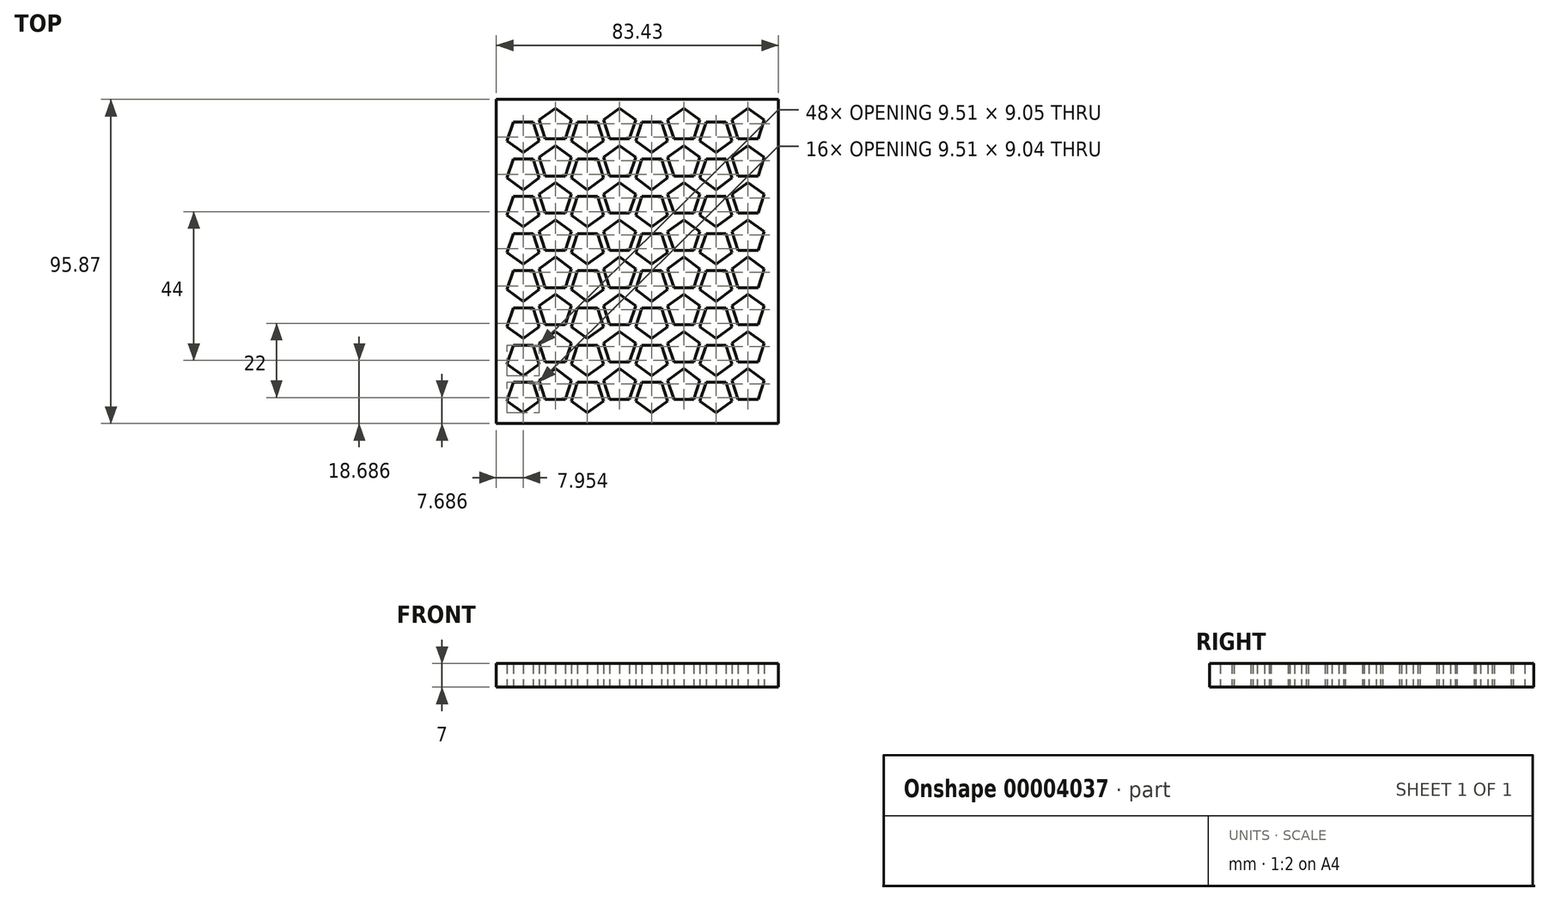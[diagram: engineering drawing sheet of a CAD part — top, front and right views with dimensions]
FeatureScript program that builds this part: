
annotation { "Feature Type Name" : "Feature", "Feature Type Description" : "" }
export const myFeature = defineFeature(function(context is Context, id is Id, definition is map)
    precondition{}
    {
        {
            var Q0;
            Q0=qCreatedBy(makeId("Top.planeOp"),FACE);
            var sketch = newSketch(context, id + "F0", { "sketchPlane" : qUnion([Q0])});
            skLineSegment(sketch, "E0.bottom", {"start": v(-101.75, 60.18) * mm, "end": v(-18.32, 60.18) * mm});
            skLineSegment(sketch, "E0.top", {"start": v(-101.75, -35.69) * mm, "end": v(-18.32, -35.69) * mm});
            skLineSegment(sketch, "E0.left", {"start": v(-101.75, 60.18) * mm, "end": v(-101.75, -35.69) * mm});
            skLineSegment(sketch, "E0.right", {"start": v(-18.32, 60.18) * mm, "end": v(-18.32, -35.69) * mm});
            skCircle(sketch, "E1.cCircle", {"center": v(-93.8, 49.47) * mm, "radius": 5 * mm, "construction": true});
            skLineSegment(sketch, "E1.0", {"start": v(-93.8, 44.47) * mm, "end": v(-98.55, 47.93) * mm});
            skLineSegment(sketch, "E1.1", {"start": v(-98.55, 47.93) * mm, "end": v(-96.73, 53.52) * mm});
            skLineSegment(sketch, "E1.2", {"start": v(-96.73, 53.52) * mm, "end": v(-90.86, 53.52) * mm});
            skLineSegment(sketch, "E1.3", {"start": v(-90.86, 53.52) * mm, "end": v(-89.04, 47.93) * mm});
            skLineSegment(sketch, "E1.4", {"start": v(-89.04, 47.93) * mm, "end": v(-93.8, 44.47) * mm});
            skLineSegment(sketch, "E2", {"start": v(-93.8, 49.47) * mm, "end": v(-93.8, 0) * mm, "construction": true});
            skCircle(sketch, "E3.cCircle", {"center": v(-84.3, 52.56) * mm, "radius": 5 * mm, "construction": true});
            skLineSegment(sketch, "E3.0", {"start": v(-87.23, 48.51) * mm, "end": v(-89.05, 54.1) * mm});
            skLineSegment(sketch, "E3.1", {"start": v(-89.05, 54.1) * mm, "end": v(-84.3, 57.56) * mm});
            skLineSegment(sketch, "E3.2", {"start": v(-84.3, 57.56) * mm, "end": v(-79.54, 54.1) * mm});
            skLineSegment(sketch, "E3.3", {"start": v(-79.54, 54.1) * mm, "end": v(-81.36, 48.51) * mm});
            skLineSegment(sketch, "E3.4", {"start": v(-81.36, 48.51) * mm, "end": v(-87.23, 48.51) * mm});
            skLineSegment(sketch, "E4", {"start": v(-93.8, 49.47) * mm, "end": v(-84.3, 52.56) * mm, "construction": true});
            skLineSegment(sketch, "E5", {"start": v(-90.86, 53.52) * mm, "end": v(-89.05, 54.1) * mm, "construction": true});
            skLineSegment(sketch, "E6.0.1.0", {"start": v(-98.55, 36.93) * mm, "end": v(-96.73, 42.52) * mm});
            skLineSegment(sketch, "E6.0.1.1", {"start": v(-96.73, 42.52) * mm, "end": v(-90.86, 42.52) * mm});
            skLineSegment(sketch, "E6.0.1.2", {"start": v(-90.86, 42.52) * mm, "end": v(-89.04, 36.93) * mm});
            skLineSegment(sketch, "E6.0.1.3", {"start": v(-89.04, 36.93) * mm, "end": v(-93.8, 33.47) * mm});
            skLineSegment(sketch, "E6.0.1.4", {"start": v(-93.8, 33.47) * mm, "end": v(-98.55, 36.93) * mm});
            skLineSegment(sketch, "E6.0.1.5", {"start": v(-87.23, 37.51) * mm, "end": v(-89.05, 43.1) * mm});
            skLineSegment(sketch, "E6.0.1.6", {"start": v(-89.05, 43.1) * mm, "end": v(-84.3, 46.56) * mm});
            skLineSegment(sketch, "E6.0.1.7", {"start": v(-84.3, 46.56) * mm, "end": v(-79.54, 43.1) * mm});
            skLineSegment(sketch, "E6.0.1.8", {"start": v(-79.54, 43.1) * mm, "end": v(-81.36, 37.51) * mm});
            skLineSegment(sketch, "E6.0.1.9", {"start": v(-81.36, 37.51) * mm, "end": v(-87.23, 37.51) * mm});
            skLineSegment(sketch, "E6.0.2.0", {"start": v(-98.55, 25.93) * mm, "end": v(-96.73, 31.52) * mm});
            skLineSegment(sketch, "E6.0.2.1", {"start": v(-96.73, 31.52) * mm, "end": v(-90.86, 31.52) * mm});
            skLineSegment(sketch, "E6.0.2.2", {"start": v(-90.86, 31.52) * mm, "end": v(-89.04, 25.93) * mm});
            skLineSegment(sketch, "E6.0.2.3", {"start": v(-89.04, 25.93) * mm, "end": v(-93.8, 22.47) * mm});
            skLineSegment(sketch, "E6.0.2.4", {"start": v(-93.8, 22.47) * mm, "end": v(-98.55, 25.93) * mm});
            skLineSegment(sketch, "E6.0.2.5", {"start": v(-87.23, 26.51) * mm, "end": v(-89.05, 32.1) * mm});
            skLineSegment(sketch, "E6.0.2.6", {"start": v(-89.05, 32.1) * mm, "end": v(-84.3, 35.56) * mm});
            skLineSegment(sketch, "E6.0.2.7", {"start": v(-84.3, 35.56) * mm, "end": v(-79.54, 32.1) * mm});
            skLineSegment(sketch, "E6.0.2.8", {"start": v(-79.54, 32.1) * mm, "end": v(-81.36, 26.51) * mm});
            skLineSegment(sketch, "E6.0.2.9", {"start": v(-81.36, 26.51) * mm, "end": v(-87.23, 26.51) * mm});
            skLineSegment(sketch, "E6.0.3.0", {"start": v(-98.55, 14.93) * mm, "end": v(-96.73, 20.52) * mm});
            skLineSegment(sketch, "E6.0.3.1", {"start": v(-96.73, 20.52) * mm, "end": v(-90.86, 20.52) * mm});
            skLineSegment(sketch, "E6.0.3.2", {"start": v(-90.86, 20.52) * mm, "end": v(-89.04, 14.93) * mm});
            skLineSegment(sketch, "E6.0.3.3", {"start": v(-89.04, 14.93) * mm, "end": v(-93.8, 11.47) * mm});
            skLineSegment(sketch, "E6.0.3.4", {"start": v(-93.8, 11.47) * mm, "end": v(-98.55, 14.93) * mm});
            skLineSegment(sketch, "E6.0.3.5", {"start": v(-87.23, 15.51) * mm, "end": v(-89.05, 21.1) * mm});
            skLineSegment(sketch, "E6.0.3.6", {"start": v(-89.05, 21.1) * mm, "end": v(-84.3, 24.56) * mm});
            skLineSegment(sketch, "E6.0.3.7", {"start": v(-84.3, 24.56) * mm, "end": v(-79.54, 21.1) * mm});
            skLineSegment(sketch, "E6.0.3.8", {"start": v(-79.54, 21.1) * mm, "end": v(-81.36, 15.51) * mm});
            skLineSegment(sketch, "E6.0.3.9", {"start": v(-81.36, 15.51) * mm, "end": v(-87.23, 15.51) * mm});
            skLineSegment(sketch, "E6.0.4.0", {"start": v(-98.55, 3.93) * mm, "end": v(-96.73, 9.52) * mm});
            skLineSegment(sketch, "E6.0.4.1", {"start": v(-96.73, 9.52) * mm, "end": v(-90.86, 9.52) * mm});
            skLineSegment(sketch, "E6.0.4.2", {"start": v(-90.86, 9.52) * mm, "end": v(-89.04, 3.93) * mm});
            skLineSegment(sketch, "E6.0.4.3", {"start": v(-89.04, 3.93) * mm, "end": v(-93.8, 0.47) * mm});
            skLineSegment(sketch, "E6.0.4.4", {"start": v(-93.8, 0.47) * mm, "end": v(-98.55, 3.93) * mm});
            skLineSegment(sketch, "E6.0.4.5", {"start": v(-87.23, 4.51) * mm, "end": v(-89.05, 10.1) * mm});
            skLineSegment(sketch, "E6.0.4.6", {"start": v(-89.05, 10.1) * mm, "end": v(-84.3, 13.56) * mm});
            skLineSegment(sketch, "E6.0.4.7", {"start": v(-84.3, 13.56) * mm, "end": v(-79.54, 10.1) * mm});
            skLineSegment(sketch, "E6.0.4.8", {"start": v(-79.54, 10.1) * mm, "end": v(-81.36, 4.51) * mm});
            skLineSegment(sketch, "E6.0.4.9", {"start": v(-81.36, 4.51) * mm, "end": v(-87.23, 4.51) * mm});
            skLineSegment(sketch, "E6.0.5.0", {"start": v(-98.55, -7.07) * mm, "end": v(-96.73, -1.48) * mm});
            skLineSegment(sketch, "E6.0.5.1", {"start": v(-96.73, -1.48) * mm, "end": v(-90.86, -1.48) * mm});
            skLineSegment(sketch, "E6.0.5.2", {"start": v(-90.86, -1.48) * mm, "end": v(-89.04, -7.07) * mm});
            skLineSegment(sketch, "E6.0.5.3", {"start": v(-89.04, -7.07) * mm, "end": v(-93.8, -10.53) * mm});
            skLineSegment(sketch, "E6.0.5.4", {"start": v(-93.8, -10.53) * mm, "end": v(-98.55, -7.07) * mm});
            skLineSegment(sketch, "E6.0.5.5", {"start": v(-87.23, -6.49) * mm, "end": v(-89.05, -0.9) * mm});
            skLineSegment(sketch, "E6.0.5.6", {"start": v(-89.05, -0.9) * mm, "end": v(-84.3, 2.56) * mm});
            skLineSegment(sketch, "E6.0.5.7", {"start": v(-84.3, 2.56) * mm, "end": v(-79.54, -0.9) * mm});
            skLineSegment(sketch, "E6.0.5.8", {"start": v(-79.54, -0.9) * mm, "end": v(-81.36, -6.49) * mm});
            skLineSegment(sketch, "E6.0.5.9", {"start": v(-81.36, -6.49) * mm, "end": v(-87.23, -6.49) * mm});
            skLineSegment(sketch, "E6.0.6.0", {"start": v(-98.55, -18.07) * mm, "end": v(-96.73, -12.48) * mm});
            skLineSegment(sketch, "E6.0.6.1", {"start": v(-96.73, -12.48) * mm, "end": v(-90.86, -12.48) * mm});
            skLineSegment(sketch, "E6.0.6.2", {"start": v(-90.86, -12.48) * mm, "end": v(-89.04, -18.07) * mm});
            skLineSegment(sketch, "E6.0.6.3", {"start": v(-89.04, -18.07) * mm, "end": v(-93.8, -21.53) * mm});
            skLineSegment(sketch, "E6.0.6.4", {"start": v(-93.8, -21.53) * mm, "end": v(-98.55, -18.07) * mm});
            skLineSegment(sketch, "E6.0.6.5", {"start": v(-87.23, -17.49) * mm, "end": v(-89.05, -11.9) * mm});
            skLineSegment(sketch, "E6.0.6.6", {"start": v(-89.05, -11.9) * mm, "end": v(-84.3, -8.44) * mm});
            skLineSegment(sketch, "E6.0.6.7", {"start": v(-84.3, -8.44) * mm, "end": v(-79.54, -11.9) * mm});
            skLineSegment(sketch, "E6.0.6.8", {"start": v(-79.54, -11.9) * mm, "end": v(-81.36, -17.49) * mm});
            skLineSegment(sketch, "E6.0.6.9", {"start": v(-81.36, -17.49) * mm, "end": v(-87.23, -17.49) * mm});
            skLineSegment(sketch, "E6.0.7.0", {"start": v(-98.55, -29.07) * mm, "end": v(-96.73, -23.48) * mm});
            skLineSegment(sketch, "E6.0.7.1", {"start": v(-96.73, -23.48) * mm, "end": v(-90.86, -23.48) * mm});
            skLineSegment(sketch, "E6.0.7.2", {"start": v(-90.86, -23.48) * mm, "end": v(-89.04, -29.07) * mm});
            skLineSegment(sketch, "E6.0.7.3", {"start": v(-89.04, -29.07) * mm, "end": v(-93.8, -32.53) * mm});
            skLineSegment(sketch, "E6.0.7.4", {"start": v(-93.8, -32.53) * mm, "end": v(-98.55, -29.07) * mm});
            skLineSegment(sketch, "E6.0.7.5", {"start": v(-87.23, -28.49) * mm, "end": v(-89.05, -22.9) * mm});
            skLineSegment(sketch, "E6.0.7.6", {"start": v(-89.05, -22.9) * mm, "end": v(-84.3, -19.44) * mm});
            skLineSegment(sketch, "E6.0.7.7", {"start": v(-84.3, -19.44) * mm, "end": v(-79.54, -22.9) * mm});
            skLineSegment(sketch, "E6.0.7.8", {"start": v(-79.54, -22.9) * mm, "end": v(-81.36, -28.49) * mm});
            skLineSegment(sketch, "E6.0.7.9", {"start": v(-81.36, -28.49) * mm, "end": v(-87.23, -28.49) * mm});
            skLineSegment(sketch, "E6.1.0.0", {"start": v(-79.55, 47.93) * mm, "end": v(-77.73, 53.52) * mm});
            skLineSegment(sketch, "E6.1.0.1", {"start": v(-77.73, 53.52) * mm, "end": v(-71.86, 53.52) * mm});
            skLineSegment(sketch, "E6.1.0.2", {"start": v(-71.86, 53.52) * mm, "end": v(-70.04, 47.93) * mm});
            skLineSegment(sketch, "E6.1.0.3", {"start": v(-70.04, 47.93) * mm, "end": v(-74.8, 44.47) * mm});
            skLineSegment(sketch, "E6.1.0.4", {"start": v(-74.8, 44.47) * mm, "end": v(-79.55, 47.93) * mm});
            skLineSegment(sketch, "E6.1.0.5", {"start": v(-68.23, 48.51) * mm, "end": v(-70.05, 54.1) * mm});
            skLineSegment(sketch, "E6.1.0.6", {"start": v(-70.05, 54.1) * mm, "end": v(-65.3, 57.56) * mm});
            skLineSegment(sketch, "E6.1.0.7", {"start": v(-65.3, 57.56) * mm, "end": v(-60.54, 54.1) * mm});
            skLineSegment(sketch, "E6.1.0.8", {"start": v(-60.54, 54.1) * mm, "end": v(-62.36, 48.51) * mm});
            skLineSegment(sketch, "E6.1.0.9", {"start": v(-62.36, 48.51) * mm, "end": v(-68.23, 48.51) * mm});
            skLineSegment(sketch, "E6.1.1.0", {"start": v(-79.55, 36.93) * mm, "end": v(-77.73, 42.52) * mm});
            skLineSegment(sketch, "E6.1.1.1", {"start": v(-77.73, 42.52) * mm, "end": v(-71.86, 42.52) * mm});
            skLineSegment(sketch, "E6.1.1.2", {"start": v(-71.86, 42.52) * mm, "end": v(-70.04, 36.93) * mm});
            skLineSegment(sketch, "E6.1.1.3", {"start": v(-70.04, 36.93) * mm, "end": v(-74.8, 33.47) * mm});
            skLineSegment(sketch, "E6.1.1.4", {"start": v(-74.8, 33.47) * mm, "end": v(-79.55, 36.93) * mm});
            skLineSegment(sketch, "E6.1.1.5", {"start": v(-68.23, 37.51) * mm, "end": v(-70.05, 43.1) * mm});
            skLineSegment(sketch, "E6.1.1.6", {"start": v(-70.05, 43.1) * mm, "end": v(-65.3, 46.56) * mm});
            skLineSegment(sketch, "E6.1.1.7", {"start": v(-65.3, 46.56) * mm, "end": v(-60.54, 43.1) * mm});
            skLineSegment(sketch, "E6.1.1.8", {"start": v(-60.54, 43.1) * mm, "end": v(-62.36, 37.51) * mm});
            skLineSegment(sketch, "E6.1.1.9", {"start": v(-62.36, 37.51) * mm, "end": v(-68.23, 37.51) * mm});
            skLineSegment(sketch, "E6.1.2.0", {"start": v(-79.55, 25.93) * mm, "end": v(-77.73, 31.52) * mm});
            skLineSegment(sketch, "E6.1.2.1", {"start": v(-77.73, 31.52) * mm, "end": v(-71.86, 31.52) * mm});
            skLineSegment(sketch, "E6.1.2.2", {"start": v(-71.86, 31.52) * mm, "end": v(-70.04, 25.93) * mm});
            skLineSegment(sketch, "E6.1.2.3", {"start": v(-70.04, 25.93) * mm, "end": v(-74.8, 22.47) * mm});
            skLineSegment(sketch, "E6.1.2.4", {"start": v(-74.8, 22.47) * mm, "end": v(-79.55, 25.93) * mm});
            skLineSegment(sketch, "E6.1.2.5", {"start": v(-68.23, 26.51) * mm, "end": v(-70.05, 32.1) * mm});
            skLineSegment(sketch, "E6.1.2.6", {"start": v(-70.05, 32.1) * mm, "end": v(-65.3, 35.56) * mm});
            skLineSegment(sketch, "E6.1.2.7", {"start": v(-65.3, 35.56) * mm, "end": v(-60.54, 32.1) * mm});
            skLineSegment(sketch, "E6.1.2.8", {"start": v(-60.54, 32.1) * mm, "end": v(-62.36, 26.51) * mm});
            skLineSegment(sketch, "E6.1.2.9", {"start": v(-62.36, 26.51) * mm, "end": v(-68.23, 26.51) * mm});
            skLineSegment(sketch, "E6.1.3.0", {"start": v(-79.55, 14.93) * mm, "end": v(-77.73, 20.52) * mm});
            skLineSegment(sketch, "E6.1.3.1", {"start": v(-77.73, 20.52) * mm, "end": v(-71.86, 20.52) * mm});
            skLineSegment(sketch, "E6.1.3.2", {"start": v(-71.86, 20.52) * mm, "end": v(-70.04, 14.93) * mm});
            skLineSegment(sketch, "E6.1.3.3", {"start": v(-70.04, 14.93) * mm, "end": v(-74.8, 11.47) * mm});
            skLineSegment(sketch, "E6.1.3.4", {"start": v(-74.8, 11.47) * mm, "end": v(-79.55, 14.93) * mm});
            skLineSegment(sketch, "E6.1.3.5", {"start": v(-68.23, 15.51) * mm, "end": v(-70.05, 21.1) * mm});
            skLineSegment(sketch, "E6.1.3.6", {"start": v(-70.05, 21.1) * mm, "end": v(-65.3, 24.56) * mm});
            skLineSegment(sketch, "E6.1.3.7", {"start": v(-65.3, 24.56) * mm, "end": v(-60.54, 21.1) * mm});
            skLineSegment(sketch, "E6.1.3.8", {"start": v(-60.54, 21.1) * mm, "end": v(-62.36, 15.51) * mm});
            skLineSegment(sketch, "E6.1.3.9", {"start": v(-62.36, 15.51) * mm, "end": v(-68.23, 15.51) * mm});
            skLineSegment(sketch, "E6.1.4.0", {"start": v(-79.55, 3.93) * mm, "end": v(-77.73, 9.52) * mm});
            skLineSegment(sketch, "E6.1.4.1", {"start": v(-77.73, 9.52) * mm, "end": v(-71.86, 9.52) * mm});
            skLineSegment(sketch, "E6.1.4.2", {"start": v(-71.86, 9.52) * mm, "end": v(-70.04, 3.93) * mm});
            skLineSegment(sketch, "E6.1.4.3", {"start": v(-70.04, 3.93) * mm, "end": v(-74.8, 0.47) * mm});
            skLineSegment(sketch, "E6.1.4.4", {"start": v(-74.8, 0.47) * mm, "end": v(-79.55, 3.93) * mm});
            skLineSegment(sketch, "E6.1.4.5", {"start": v(-68.23, 4.51) * mm, "end": v(-70.05, 10.1) * mm});
            skLineSegment(sketch, "E6.1.4.6", {"start": v(-70.05, 10.1) * mm, "end": v(-65.3, 13.56) * mm});
            skLineSegment(sketch, "E6.1.4.7", {"start": v(-65.3, 13.56) * mm, "end": v(-60.54, 10.1) * mm});
            skLineSegment(sketch, "E6.1.4.8", {"start": v(-60.54, 10.1) * mm, "end": v(-62.36, 4.51) * mm});
            skLineSegment(sketch, "E6.1.4.9", {"start": v(-62.36, 4.51) * mm, "end": v(-68.23, 4.51) * mm});
            skLineSegment(sketch, "E6.1.5.0", {"start": v(-79.55, -7.07) * mm, "end": v(-77.73, -1.48) * mm});
            skLineSegment(sketch, "E6.1.5.1", {"start": v(-77.73, -1.48) * mm, "end": v(-71.86, -1.48) * mm});
            skLineSegment(sketch, "E6.1.5.2", {"start": v(-71.86, -1.48) * mm, "end": v(-70.04, -7.07) * mm});
            skLineSegment(sketch, "E6.1.5.3", {"start": v(-70.04, -7.07) * mm, "end": v(-74.8, -10.53) * mm});
            skLineSegment(sketch, "E6.1.5.4", {"start": v(-74.8, -10.53) * mm, "end": v(-79.55, -7.07) * mm});
            skLineSegment(sketch, "E6.1.5.5", {"start": v(-68.23, -6.49) * mm, "end": v(-70.05, -0.9) * mm});
            skLineSegment(sketch, "E6.1.5.6", {"start": v(-70.05, -0.9) * mm, "end": v(-65.3, 2.56) * mm});
            skLineSegment(sketch, "E6.1.5.7", {"start": v(-65.3, 2.56) * mm, "end": v(-60.54, -0.9) * mm});
            skLineSegment(sketch, "E6.1.5.8", {"start": v(-60.54, -0.9) * mm, "end": v(-62.36, -6.49) * mm});
            skLineSegment(sketch, "E6.1.5.9", {"start": v(-62.36, -6.49) * mm, "end": v(-68.23, -6.49) * mm});
            skLineSegment(sketch, "E6.1.6.0", {"start": v(-79.55, -18.07) * mm, "end": v(-77.73, -12.48) * mm});
            skLineSegment(sketch, "E6.1.6.1", {"start": v(-77.73, -12.48) * mm, "end": v(-71.86, -12.48) * mm});
            skLineSegment(sketch, "E6.1.6.2", {"start": v(-71.86, -12.48) * mm, "end": v(-70.04, -18.07) * mm});
            skLineSegment(sketch, "E6.1.6.3", {"start": v(-70.04, -18.07) * mm, "end": v(-74.8, -21.53) * mm});
            skLineSegment(sketch, "E6.1.6.4", {"start": v(-74.8, -21.53) * mm, "end": v(-79.55, -18.07) * mm});
            skLineSegment(sketch, "E6.1.6.5", {"start": v(-68.23, -17.49) * mm, "end": v(-70.05, -11.9) * mm});
            skLineSegment(sketch, "E6.1.6.6", {"start": v(-70.05, -11.9) * mm, "end": v(-65.3, -8.44) * mm});
            skLineSegment(sketch, "E6.1.6.7", {"start": v(-65.3, -8.44) * mm, "end": v(-60.54, -11.9) * mm});
            skLineSegment(sketch, "E6.1.6.8", {"start": v(-60.54, -11.9) * mm, "end": v(-62.36, -17.49) * mm});
            skLineSegment(sketch, "E6.1.6.9", {"start": v(-62.36, -17.49) * mm, "end": v(-68.23, -17.49) * mm});
            skLineSegment(sketch, "E6.1.7.0", {"start": v(-79.55, -29.07) * mm, "end": v(-77.73, -23.48) * mm});
            skLineSegment(sketch, "E6.1.7.1", {"start": v(-77.73, -23.48) * mm, "end": v(-71.86, -23.48) * mm});
            skLineSegment(sketch, "E6.1.7.2", {"start": v(-71.86, -23.48) * mm, "end": v(-70.04, -29.07) * mm});
            skLineSegment(sketch, "E6.1.7.3", {"start": v(-70.04, -29.07) * mm, "end": v(-74.8, -32.53) * mm});
            skLineSegment(sketch, "E6.1.7.4", {"start": v(-74.8, -32.53) * mm, "end": v(-79.55, -29.07) * mm});
            skLineSegment(sketch, "E6.1.7.5", {"start": v(-68.23, -28.49) * mm, "end": v(-70.05, -22.9) * mm});
            skLineSegment(sketch, "E6.1.7.6", {"start": v(-70.05, -22.9) * mm, "end": v(-65.3, -19.44) * mm});
            skLineSegment(sketch, "E6.1.7.7", {"start": v(-65.3, -19.44) * mm, "end": v(-60.54, -22.9) * mm});
            skLineSegment(sketch, "E6.1.7.8", {"start": v(-60.54, -22.9) * mm, "end": v(-62.36, -28.49) * mm});
            skLineSegment(sketch, "E6.1.7.9", {"start": v(-62.36, -28.49) * mm, "end": v(-68.23, -28.49) * mm});
            skLineSegment(sketch, "E6.2.0.0", {"start": v(-60.55, 47.93) * mm, "end": v(-58.73, 53.52) * mm});
            skLineSegment(sketch, "E6.2.0.1", {"start": v(-58.73, 53.52) * mm, "end": v(-52.86, 53.52) * mm});
            skLineSegment(sketch, "E6.2.0.2", {"start": v(-52.86, 53.52) * mm, "end": v(-51.04, 47.93) * mm});
            skLineSegment(sketch, "E6.2.0.3", {"start": v(-51.04, 47.93) * mm, "end": v(-55.8, 44.47) * mm});
            skLineSegment(sketch, "E6.2.0.4", {"start": v(-55.8, 44.47) * mm, "end": v(-60.55, 47.93) * mm});
            skLineSegment(sketch, "E6.2.0.5", {"start": v(-49.23, 48.51) * mm, "end": v(-51.05, 54.1) * mm});
            skLineSegment(sketch, "E6.2.0.6", {"start": v(-51.05, 54.1) * mm, "end": v(-46.3, 57.56) * mm});
            skLineSegment(sketch, "E6.2.0.7", {"start": v(-46.3, 57.56) * mm, "end": v(-41.54, 54.1) * mm});
            skLineSegment(sketch, "E6.2.0.8", {"start": v(-41.54, 54.1) * mm, "end": v(-43.36, 48.51) * mm});
            skLineSegment(sketch, "E6.2.0.9", {"start": v(-43.36, 48.51) * mm, "end": v(-49.23, 48.51) * mm});
            skLineSegment(sketch, "E6.2.1.0", {"start": v(-60.55, 36.93) * mm, "end": v(-58.73, 42.52) * mm});
            skLineSegment(sketch, "E6.2.1.1", {"start": v(-58.73, 42.52) * mm, "end": v(-52.86, 42.52) * mm});
            skLineSegment(sketch, "E6.2.1.2", {"start": v(-52.86, 42.52) * mm, "end": v(-51.04, 36.93) * mm});
            skLineSegment(sketch, "E6.2.1.3", {"start": v(-51.04, 36.93) * mm, "end": v(-55.8, 33.47) * mm});
            skLineSegment(sketch, "E6.2.1.4", {"start": v(-55.8, 33.47) * mm, "end": v(-60.55, 36.93) * mm});
            skLineSegment(sketch, "E6.2.1.5", {"start": v(-49.23, 37.51) * mm, "end": v(-51.05, 43.1) * mm});
            skLineSegment(sketch, "E6.2.1.6", {"start": v(-51.05, 43.1) * mm, "end": v(-46.3, 46.56) * mm});
            skLineSegment(sketch, "E6.2.1.7", {"start": v(-46.3, 46.56) * mm, "end": v(-41.54, 43.1) * mm});
            skLineSegment(sketch, "E6.2.1.8", {"start": v(-41.54, 43.1) * mm, "end": v(-43.36, 37.51) * mm});
            skLineSegment(sketch, "E6.2.1.9", {"start": v(-43.36, 37.51) * mm, "end": v(-49.23, 37.51) * mm});
            skLineSegment(sketch, "E6.2.2.0", {"start": v(-60.55, 25.93) * mm, "end": v(-58.73, 31.52) * mm});
            skLineSegment(sketch, "E6.2.2.1", {"start": v(-58.73, 31.52) * mm, "end": v(-52.86, 31.52) * mm});
            skLineSegment(sketch, "E6.2.2.2", {"start": v(-52.86, 31.52) * mm, "end": v(-51.04, 25.93) * mm});
            skLineSegment(sketch, "E6.2.2.3", {"start": v(-51.04, 25.93) * mm, "end": v(-55.8, 22.47) * mm});
            skLineSegment(sketch, "E6.2.2.4", {"start": v(-55.8, 22.47) * mm, "end": v(-60.55, 25.93) * mm});
            skLineSegment(sketch, "E6.2.2.5", {"start": v(-49.23, 26.51) * mm, "end": v(-51.05, 32.1) * mm});
            skLineSegment(sketch, "E6.2.2.6", {"start": v(-51.05, 32.1) * mm, "end": v(-46.3, 35.56) * mm});
            skLineSegment(sketch, "E6.2.2.7", {"start": v(-46.3, 35.56) * mm, "end": v(-41.54, 32.1) * mm});
            skLineSegment(sketch, "E6.2.2.8", {"start": v(-41.54, 32.1) * mm, "end": v(-43.36, 26.51) * mm});
            skLineSegment(sketch, "E6.2.2.9", {"start": v(-43.36, 26.51) * mm, "end": v(-49.23, 26.51) * mm});
            skLineSegment(sketch, "E6.2.3.0", {"start": v(-60.55, 14.93) * mm, "end": v(-58.73, 20.52) * mm});
            skLineSegment(sketch, "E6.2.3.1", {"start": v(-58.73, 20.52) * mm, "end": v(-52.86, 20.52) * mm});
            skLineSegment(sketch, "E6.2.3.2", {"start": v(-52.86, 20.52) * mm, "end": v(-51.04, 14.93) * mm});
            skLineSegment(sketch, "E6.2.3.3", {"start": v(-51.04, 14.93) * mm, "end": v(-55.8, 11.47) * mm});
            skLineSegment(sketch, "E6.2.3.4", {"start": v(-55.8, 11.47) * mm, "end": v(-60.55, 14.93) * mm});
            skLineSegment(sketch, "E6.2.3.5", {"start": v(-49.23, 15.51) * mm, "end": v(-51.05, 21.1) * mm});
            skLineSegment(sketch, "E6.2.3.6", {"start": v(-51.05, 21.1) * mm, "end": v(-46.3, 24.56) * mm});
            skLineSegment(sketch, "E6.2.3.7", {"start": v(-46.3, 24.56) * mm, "end": v(-41.54, 21.1) * mm});
            skLineSegment(sketch, "E6.2.3.8", {"start": v(-41.54, 21.1) * mm, "end": v(-43.36, 15.51) * mm});
            skLineSegment(sketch, "E6.2.3.9", {"start": v(-43.36, 15.51) * mm, "end": v(-49.23, 15.51) * mm});
            skLineSegment(sketch, "E6.2.4.0", {"start": v(-60.55, 3.93) * mm, "end": v(-58.73, 9.52) * mm});
            skLineSegment(sketch, "E6.2.4.1", {"start": v(-58.73, 9.52) * mm, "end": v(-52.86, 9.52) * mm});
            skLineSegment(sketch, "E6.2.4.2", {"start": v(-52.86, 9.52) * mm, "end": v(-51.04, 3.93) * mm});
            skLineSegment(sketch, "E6.2.4.3", {"start": v(-51.04, 3.93) * mm, "end": v(-55.8, 0.47) * mm});
            skLineSegment(sketch, "E6.2.4.4", {"start": v(-55.8, 0.47) * mm, "end": v(-60.55, 3.93) * mm});
            skLineSegment(sketch, "E6.2.4.5", {"start": v(-49.23, 4.51) * mm, "end": v(-51.05, 10.1) * mm});
            skLineSegment(sketch, "E6.2.4.6", {"start": v(-51.05, 10.1) * mm, "end": v(-46.3, 13.56) * mm});
            skLineSegment(sketch, "E6.2.4.7", {"start": v(-46.3, 13.56) * mm, "end": v(-41.54, 10.1) * mm});
            skLineSegment(sketch, "E6.2.4.8", {"start": v(-41.54, 10.1) * mm, "end": v(-43.36, 4.51) * mm});
            skLineSegment(sketch, "E6.2.4.9", {"start": v(-43.36, 4.51) * mm, "end": v(-49.23, 4.51) * mm});
            skLineSegment(sketch, "E6.2.5.0", {"start": v(-60.55, -7.07) * mm, "end": v(-58.73, -1.48) * mm});
            skLineSegment(sketch, "E6.2.5.1", {"start": v(-58.73, -1.48) * mm, "end": v(-52.86, -1.48) * mm});
            skLineSegment(sketch, "E6.2.5.2", {"start": v(-52.86, -1.48) * mm, "end": v(-51.04, -7.07) * mm});
            skLineSegment(sketch, "E6.2.5.3", {"start": v(-51.04, -7.07) * mm, "end": v(-55.8, -10.53) * mm});
            skLineSegment(sketch, "E6.2.5.4", {"start": v(-55.8, -10.53) * mm, "end": v(-60.55, -7.07) * mm});
            skLineSegment(sketch, "E6.2.5.5", {"start": v(-49.23, -6.49) * mm, "end": v(-51.05, -0.9) * mm});
            skLineSegment(sketch, "E6.2.5.6", {"start": v(-51.05, -0.9) * mm, "end": v(-46.3, 2.56) * mm});
            skLineSegment(sketch, "E6.2.5.7", {"start": v(-46.3, 2.56) * mm, "end": v(-41.54, -0.9) * mm});
            skLineSegment(sketch, "E6.2.5.8", {"start": v(-41.54, -0.9) * mm, "end": v(-43.36, -6.49) * mm});
            skLineSegment(sketch, "E6.2.5.9", {"start": v(-43.36, -6.49) * mm, "end": v(-49.23, -6.49) * mm});
            skLineSegment(sketch, "E6.2.6.0", {"start": v(-60.55, -18.07) * mm, "end": v(-58.73, -12.48) * mm});
            skLineSegment(sketch, "E6.2.6.1", {"start": v(-58.73, -12.48) * mm, "end": v(-52.86, -12.48) * mm});
            skLineSegment(sketch, "E6.2.6.2", {"start": v(-52.86, -12.48) * mm, "end": v(-51.04, -18.07) * mm});
            skLineSegment(sketch, "E6.2.6.3", {"start": v(-51.04, -18.07) * mm, "end": v(-55.8, -21.53) * mm});
            skLineSegment(sketch, "E6.2.6.4", {"start": v(-55.8, -21.53) * mm, "end": v(-60.55, -18.07) * mm});
            skLineSegment(sketch, "E6.2.6.5", {"start": v(-49.23, -17.49) * mm, "end": v(-51.05, -11.9) * mm});
            skLineSegment(sketch, "E6.2.6.6", {"start": v(-51.05, -11.9) * mm, "end": v(-46.3, -8.44) * mm});
            skLineSegment(sketch, "E6.2.6.7", {"start": v(-46.3, -8.44) * mm, "end": v(-41.54, -11.9) * mm});
            skLineSegment(sketch, "E6.2.6.8", {"start": v(-41.54, -11.9) * mm, "end": v(-43.36, -17.49) * mm});
            skLineSegment(sketch, "E6.2.6.9", {"start": v(-43.36, -17.49) * mm, "end": v(-49.23, -17.49) * mm});
            skLineSegment(sketch, "E6.2.7.0", {"start": v(-60.55, -29.07) * mm, "end": v(-58.73, -23.48) * mm});
            skLineSegment(sketch, "E6.2.7.1", {"start": v(-58.73, -23.48) * mm, "end": v(-52.86, -23.48) * mm});
            skLineSegment(sketch, "E6.2.7.2", {"start": v(-52.86, -23.48) * mm, "end": v(-51.04, -29.07) * mm});
            skLineSegment(sketch, "E6.2.7.3", {"start": v(-51.04, -29.07) * mm, "end": v(-55.8, -32.53) * mm});
            skLineSegment(sketch, "E6.2.7.4", {"start": v(-55.8, -32.53) * mm, "end": v(-60.55, -29.07) * mm});
            skLineSegment(sketch, "E6.2.7.5", {"start": v(-49.23, -28.49) * mm, "end": v(-51.05, -22.9) * mm});
            skLineSegment(sketch, "E6.2.7.6", {"start": v(-51.05, -22.9) * mm, "end": v(-46.3, -19.44) * mm});
            skLineSegment(sketch, "E6.2.7.7", {"start": v(-46.3, -19.44) * mm, "end": v(-41.54, -22.9) * mm});
            skLineSegment(sketch, "E6.2.7.8", {"start": v(-41.54, -22.9) * mm, "end": v(-43.36, -28.49) * mm});
            skLineSegment(sketch, "E6.2.7.9", {"start": v(-43.36, -28.49) * mm, "end": v(-49.23, -28.49) * mm});
            skLineSegment(sketch, "E6.3.0.0", {"start": v(-41.55, 47.93) * mm, "end": v(-39.73, 53.52) * mm});
            skLineSegment(sketch, "E6.3.0.1", {"start": v(-39.73, 53.52) * mm, "end": v(-33.86, 53.52) * mm});
            skLineSegment(sketch, "E6.3.0.2", {"start": v(-33.86, 53.52) * mm, "end": v(-32.04, 47.93) * mm});
            skLineSegment(sketch, "E6.3.0.3", {"start": v(-32.04, 47.93) * mm, "end": v(-36.8, 44.47) * mm});
            skLineSegment(sketch, "E6.3.0.4", {"start": v(-36.8, 44.47) * mm, "end": v(-41.55, 47.93) * mm});
            skLineSegment(sketch, "E6.3.0.5", {"start": v(-30.23, 48.51) * mm, "end": v(-32.05, 54.1) * mm});
            skLineSegment(sketch, "E6.3.0.6", {"start": v(-32.05, 54.1) * mm, "end": v(-27.3, 57.56) * mm});
            skLineSegment(sketch, "E6.3.0.7", {"start": v(-27.3, 57.56) * mm, "end": v(-22.54, 54.1) * mm});
            skLineSegment(sketch, "E6.3.0.8", {"start": v(-22.54, 54.1) * mm, "end": v(-24.36, 48.51) * mm});
            skLineSegment(sketch, "E6.3.0.9", {"start": v(-24.36, 48.51) * mm, "end": v(-30.23, 48.51) * mm});
            skLineSegment(sketch, "E6.3.1.0", {"start": v(-41.55, 36.93) * mm, "end": v(-39.73, 42.52) * mm});
            skLineSegment(sketch, "E6.3.1.1", {"start": v(-39.73, 42.52) * mm, "end": v(-33.86, 42.52) * mm});
            skLineSegment(sketch, "E6.3.1.2", {"start": v(-33.86, 42.52) * mm, "end": v(-32.04, 36.93) * mm});
            skLineSegment(sketch, "E6.3.1.3", {"start": v(-32.04, 36.93) * mm, "end": v(-36.8, 33.47) * mm});
            skLineSegment(sketch, "E6.3.1.4", {"start": v(-36.8, 33.47) * mm, "end": v(-41.55, 36.93) * mm});
            skLineSegment(sketch, "E6.3.1.5", {"start": v(-30.23, 37.51) * mm, "end": v(-32.05, 43.1) * mm});
            skLineSegment(sketch, "E6.3.1.6", {"start": v(-32.05, 43.1) * mm, "end": v(-27.3, 46.56) * mm});
            skLineSegment(sketch, "E6.3.1.7", {"start": v(-27.3, 46.56) * mm, "end": v(-22.54, 43.1) * mm});
            skLineSegment(sketch, "E6.3.1.8", {"start": v(-22.54, 43.1) * mm, "end": v(-24.36, 37.51) * mm});
            skLineSegment(sketch, "E6.3.1.9", {"start": v(-24.36, 37.51) * mm, "end": v(-30.23, 37.51) * mm});
            skLineSegment(sketch, "E6.3.2.0", {"start": v(-41.55, 25.93) * mm, "end": v(-39.73, 31.52) * mm});
            skLineSegment(sketch, "E6.3.2.1", {"start": v(-39.73, 31.52) * mm, "end": v(-33.86, 31.52) * mm});
            skLineSegment(sketch, "E6.3.2.2", {"start": v(-33.86, 31.52) * mm, "end": v(-32.04, 25.93) * mm});
            skLineSegment(sketch, "E6.3.2.3", {"start": v(-32.04, 25.93) * mm, "end": v(-36.8, 22.47) * mm});
            skLineSegment(sketch, "E6.3.2.4", {"start": v(-36.8, 22.47) * mm, "end": v(-41.55, 25.93) * mm});
            skLineSegment(sketch, "E6.3.2.5", {"start": v(-30.23, 26.51) * mm, "end": v(-32.05, 32.1) * mm});
            skLineSegment(sketch, "E6.3.2.6", {"start": v(-32.05, 32.1) * mm, "end": v(-27.3, 35.56) * mm});
            skLineSegment(sketch, "E6.3.2.7", {"start": v(-27.3, 35.56) * mm, "end": v(-22.54, 32.1) * mm});
            skLineSegment(sketch, "E6.3.2.8", {"start": v(-22.54, 32.1) * mm, "end": v(-24.36, 26.51) * mm});
            skLineSegment(sketch, "E6.3.2.9", {"start": v(-24.36, 26.51) * mm, "end": v(-30.23, 26.51) * mm});
            skLineSegment(sketch, "E6.3.3.0", {"start": v(-41.55, 14.93) * mm, "end": v(-39.73, 20.52) * mm});
            skLineSegment(sketch, "E6.3.3.1", {"start": v(-39.73, 20.52) * mm, "end": v(-33.86, 20.52) * mm});
            skLineSegment(sketch, "E6.3.3.2", {"start": v(-33.86, 20.52) * mm, "end": v(-32.04, 14.93) * mm});
            skLineSegment(sketch, "E6.3.3.3", {"start": v(-32.04, 14.93) * mm, "end": v(-36.8, 11.47) * mm});
            skLineSegment(sketch, "E6.3.3.4", {"start": v(-36.8, 11.47) * mm, "end": v(-41.55, 14.93) * mm});
            skLineSegment(sketch, "E6.3.3.5", {"start": v(-30.23, 15.51) * mm, "end": v(-32.05, 21.1) * mm});
            skLineSegment(sketch, "E6.3.3.6", {"start": v(-32.05, 21.1) * mm, "end": v(-27.3, 24.56) * mm});
            skLineSegment(sketch, "E6.3.3.7", {"start": v(-27.3, 24.56) * mm, "end": v(-22.54, 21.1) * mm});
            skLineSegment(sketch, "E6.3.3.8", {"start": v(-22.54, 21.1) * mm, "end": v(-24.36, 15.51) * mm});
            skLineSegment(sketch, "E6.3.3.9", {"start": v(-24.36, 15.51) * mm, "end": v(-30.23, 15.51) * mm});
            skLineSegment(sketch, "E6.3.4.0", {"start": v(-41.55, 3.93) * mm, "end": v(-39.73, 9.52) * mm});
            skLineSegment(sketch, "E6.3.4.1", {"start": v(-39.73, 9.52) * mm, "end": v(-33.86, 9.52) * mm});
            skLineSegment(sketch, "E6.3.4.2", {"start": v(-33.86, 9.52) * mm, "end": v(-32.04, 3.93) * mm});
            skLineSegment(sketch, "E6.3.4.3", {"start": v(-32.04, 3.93) * mm, "end": v(-36.8, 0.47) * mm});
            skLineSegment(sketch, "E6.3.4.4", {"start": v(-36.8, 0.47) * mm, "end": v(-41.55, 3.93) * mm});
            skLineSegment(sketch, "E6.3.4.5", {"start": v(-30.23, 4.51) * mm, "end": v(-32.05, 10.1) * mm});
            skLineSegment(sketch, "E6.3.4.6", {"start": v(-32.05, 10.1) * mm, "end": v(-27.3, 13.56) * mm});
            skLineSegment(sketch, "E6.3.4.7", {"start": v(-27.3, 13.56) * mm, "end": v(-22.54, 10.1) * mm});
            skLineSegment(sketch, "E6.3.4.8", {"start": v(-22.54, 10.1) * mm, "end": v(-24.36, 4.51) * mm});
            skLineSegment(sketch, "E6.3.4.9", {"start": v(-24.36, 4.51) * mm, "end": v(-30.23, 4.51) * mm});
            skLineSegment(sketch, "E6.3.5.0", {"start": v(-41.55, -7.07) * mm, "end": v(-39.73, -1.48) * mm});
            skLineSegment(sketch, "E6.3.5.1", {"start": v(-39.73, -1.48) * mm, "end": v(-33.86, -1.48) * mm});
            skLineSegment(sketch, "E6.3.5.2", {"start": v(-33.86, -1.48) * mm, "end": v(-32.04, -7.07) * mm});
            skLineSegment(sketch, "E6.3.5.3", {"start": v(-32.04, -7.07) * mm, "end": v(-36.8, -10.53) * mm});
            skLineSegment(sketch, "E6.3.5.4", {"start": v(-36.8, -10.53) * mm, "end": v(-41.55, -7.07) * mm});
            skLineSegment(sketch, "E6.3.5.5", {"start": v(-30.23, -6.49) * mm, "end": v(-32.05, -0.9) * mm});
            skLineSegment(sketch, "E6.3.5.6", {"start": v(-32.05, -0.9) * mm, "end": v(-27.3, 2.56) * mm});
            skLineSegment(sketch, "E6.3.5.7", {"start": v(-27.3, 2.56) * mm, "end": v(-22.54, -0.9) * mm});
            skLineSegment(sketch, "E6.3.5.8", {"start": v(-22.54, -0.9) * mm, "end": v(-24.36, -6.49) * mm});
            skLineSegment(sketch, "E6.3.5.9", {"start": v(-24.36, -6.49) * mm, "end": v(-30.23, -6.49) * mm});
            skLineSegment(sketch, "E6.3.6.0", {"start": v(-41.55, -18.07) * mm, "end": v(-39.73, -12.48) * mm});
            skLineSegment(sketch, "E6.3.6.1", {"start": v(-39.73, -12.48) * mm, "end": v(-33.86, -12.48) * mm});
            skLineSegment(sketch, "E6.3.6.2", {"start": v(-33.86, -12.48) * mm, "end": v(-32.04, -18.07) * mm});
            skLineSegment(sketch, "E6.3.6.3", {"start": v(-32.04, -18.07) * mm, "end": v(-36.8, -21.53) * mm});
            skLineSegment(sketch, "E6.3.6.4", {"start": v(-36.8, -21.53) * mm, "end": v(-41.55, -18.07) * mm});
            skLineSegment(sketch, "E6.3.6.5", {"start": v(-30.23, -17.49) * mm, "end": v(-32.05, -11.9) * mm});
            skLineSegment(sketch, "E6.3.6.6", {"start": v(-32.05, -11.9) * mm, "end": v(-27.3, -8.44) * mm});
            skLineSegment(sketch, "E6.3.6.7", {"start": v(-27.3, -8.44) * mm, "end": v(-22.54, -11.9) * mm});
            skLineSegment(sketch, "E6.3.6.8", {"start": v(-22.54, -11.9) * mm, "end": v(-24.36, -17.49) * mm});
            skLineSegment(sketch, "E6.3.6.9", {"start": v(-24.36, -17.49) * mm, "end": v(-30.23, -17.49) * mm});
            skLineSegment(sketch, "E6.3.7.0", {"start": v(-41.55, -29.07) * mm, "end": v(-39.73, -23.48) * mm});
            skLineSegment(sketch, "E6.3.7.1", {"start": v(-39.73, -23.48) * mm, "end": v(-33.86, -23.48) * mm});
            skLineSegment(sketch, "E6.3.7.2", {"start": v(-33.86, -23.48) * mm, "end": v(-32.04, -29.07) * mm});
            skLineSegment(sketch, "E6.3.7.3", {"start": v(-32.04, -29.07) * mm, "end": v(-36.8, -32.53) * mm});
            skLineSegment(sketch, "E6.3.7.4", {"start": v(-36.8, -32.53) * mm, "end": v(-41.55, -29.07) * mm});
            skLineSegment(sketch, "E6.3.7.5", {"start": v(-30.23, -28.49) * mm, "end": v(-32.05, -22.9) * mm});
            skLineSegment(sketch, "E6.3.7.6", {"start": v(-32.05, -22.9) * mm, "end": v(-27.3, -19.44) * mm});
            skLineSegment(sketch, "E6.3.7.7", {"start": v(-27.3, -19.44) * mm, "end": v(-22.54, -22.9) * mm});
            skLineSegment(sketch, "E6.3.7.8", {"start": v(-22.54, -22.9) * mm, "end": v(-24.36, -28.49) * mm});
            skLineSegment(sketch, "E6.3.7.9", {"start": v(-24.36, -28.49) * mm, "end": v(-30.23, -28.49) * mm});
            skLineSegment(sketch, "E6.direction1", {"start": v(-98.55, 47.93) * mm, "end": v(-79.55, 47.93) * mm, "construction": true});
            skLineSegment(sketch, "E6.direction2", {"start": v(-98.55, 47.93) * mm, "end": v(-98.55, 36.93) * mm, "construction": true});
            skLineSegment(sketch, "E7", {"start": v(-79.54, 54.1) * mm, "end": v(-77.73, 53.52) * mm, "construction": true});
            skSolve(sketch);
        }
        {
            var Q0;
            Q0=makeQuery(id+"F0.imprint","IMPRINT",FACE,{"disambiguationData":[TD([[makeQuery(id+"F0.imprint","IMPRINT",EDGE,{"derivedFrom":sQuery(id+"F0.wireOp",EDGE,"E0.bottom")}),-1.0]])]});
            extrude(context, id + "F1", {"entities" : qUnion([Q0]), "depth" : 7 * mm});
        }
    });
